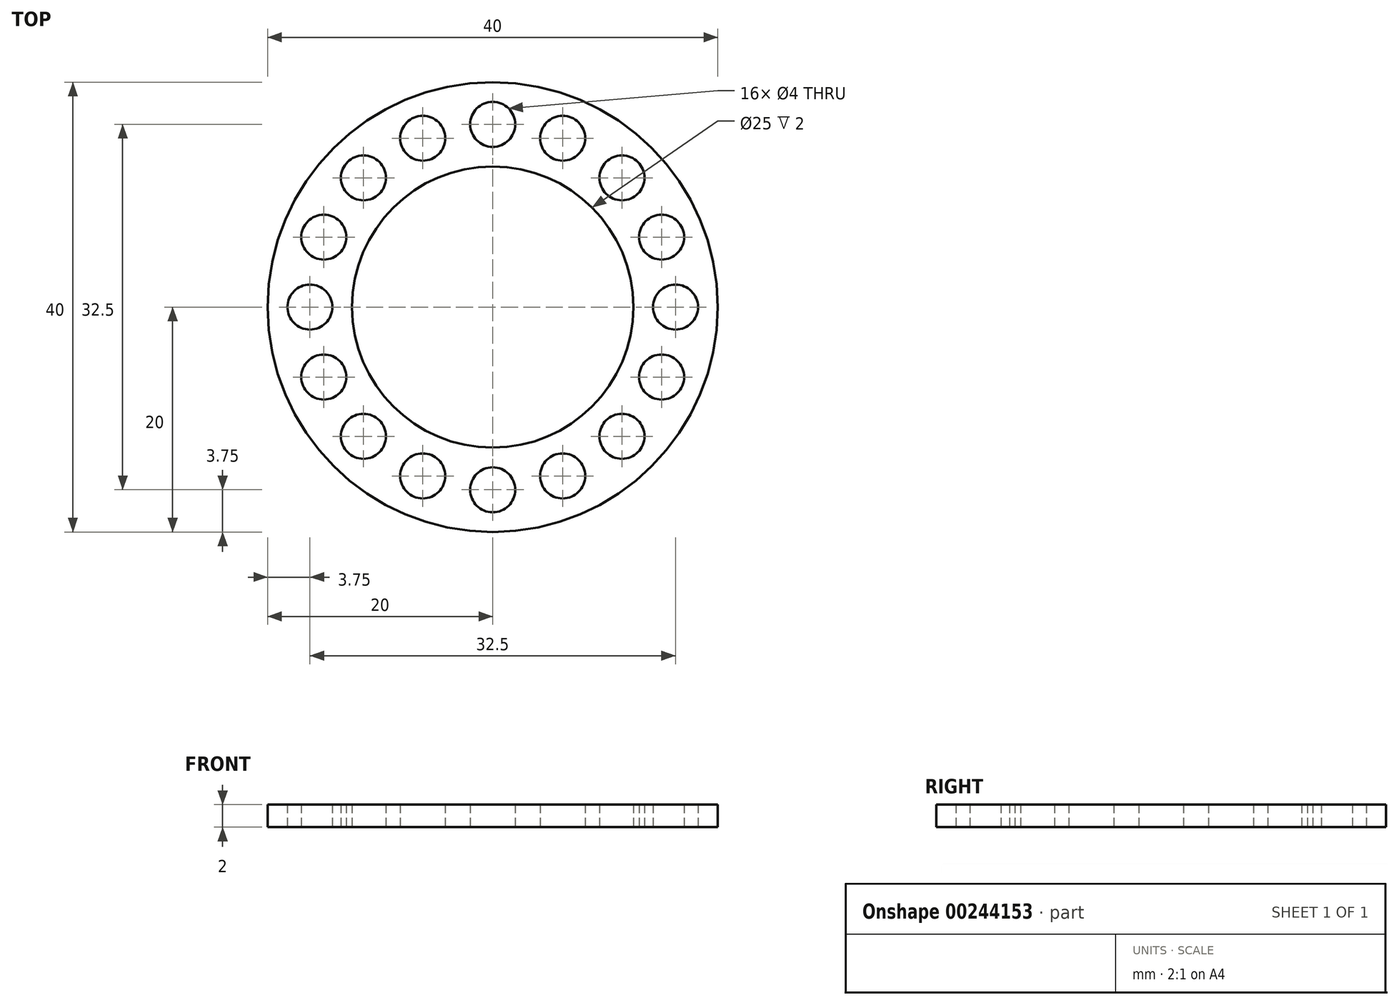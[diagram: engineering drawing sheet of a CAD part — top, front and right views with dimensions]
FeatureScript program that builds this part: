
annotation { "Feature Type Name" : "Feature", "Feature Type Description" : "" }
export const myFeature = defineFeature(function(context is Context, id is Id, definition is map)
    precondition{}
    {
        {
            var Q0;
            Q0=qCreatedBy(makeId("Top.planeOp"),FACE);
            var sketch = newSketch(context, id + "F0", { "sketchPlane" : qUnion([Q0])});
            skCircle(sketch, "E0", {"center": v(0, 0) * mm, "radius": 12.5 * mm});
            skCircle(sketch, "E1", {"center": v(0, 0) * mm, "radius": 20 * mm});
            skCircle(sketch, "E2", {"center": v(0, 16.25) * mm, "radius": 2 * mm});
            skCircle(sketch, "E3.1.0", {"center": v(-6.22, 15.01) * mm, "radius": 2 * mm});
            skCircle(sketch, "E3.2.0", {"center": v(-11.5, 11.5) * mm, "radius": 2 * mm});
            skCircle(sketch, "E4.1.3.0", {"center": v(-15.01, 6.22) * mm, "radius": 2 * mm});
            skCircle(sketch, "E4.1.4.0", {"center": v(-16.25, 0) * mm, "radius": 2 * mm});
            skCircle(sketch, "E4.1.5.0", {"center": v(-15.01, -6.22) * mm, "radius": 2 * mm});
            skCircle(sketch, "E4.1.6.0", {"center": v(-11.5, -11.5) * mm, "radius": 2 * mm});
            skCircle(sketch, "E4.1.7.0", {"center": v(-6.22, -15.01) * mm, "radius": 2 * mm});
            skCircle(sketch, "E4.1.8.0", {"center": v(0, -16.25) * mm, "radius": 2 * mm});
            skCircle(sketch, "E4.1.9.0", {"center": v(6.22, -15.01) * mm, "radius": 2 * mm});
            skCircle(sketch, "E4.1.10.0", {"center": v(11.5, -11.5) * mm, "radius": 2 * mm});
            skCircle(sketch, "E4.1.11.0", {"center": v(15.01, -6.22) * mm, "radius": 2 * mm});
            skCircle(sketch, "E4.1.12.0", {"center": v(16.25, 0) * mm, "radius": 2 * mm});
            skCircle(sketch, "E4.1.13.0", {"center": v(15.01, 6.22) * mm, "radius": 2 * mm});
            skCircle(sketch, "E4.1.14.0", {"center": v(11.5, 11.5) * mm, "radius": 2 * mm});
            skCircle(sketch, "E4.1.15.0", {"center": v(6.22, 15.01) * mm, "radius": 2 * mm});
            skSolve(sketch);
        }
        {
            var Q0;
            Q0=makeQuery(id+"F0.imprint","IMPRINT",FACE,{"disambiguationData":[TD([[makeQuery(id+"F0.imprint","IMPRINT",EDGE,{"derivedFrom":sQuery(id+"F0.wireOp",EDGE,"E0")}),-1.0]])]});
            extrude(context, id + "F1", {"entities" : qUnion([Q0]), "depth" : 2 * mm});
        }
    });
